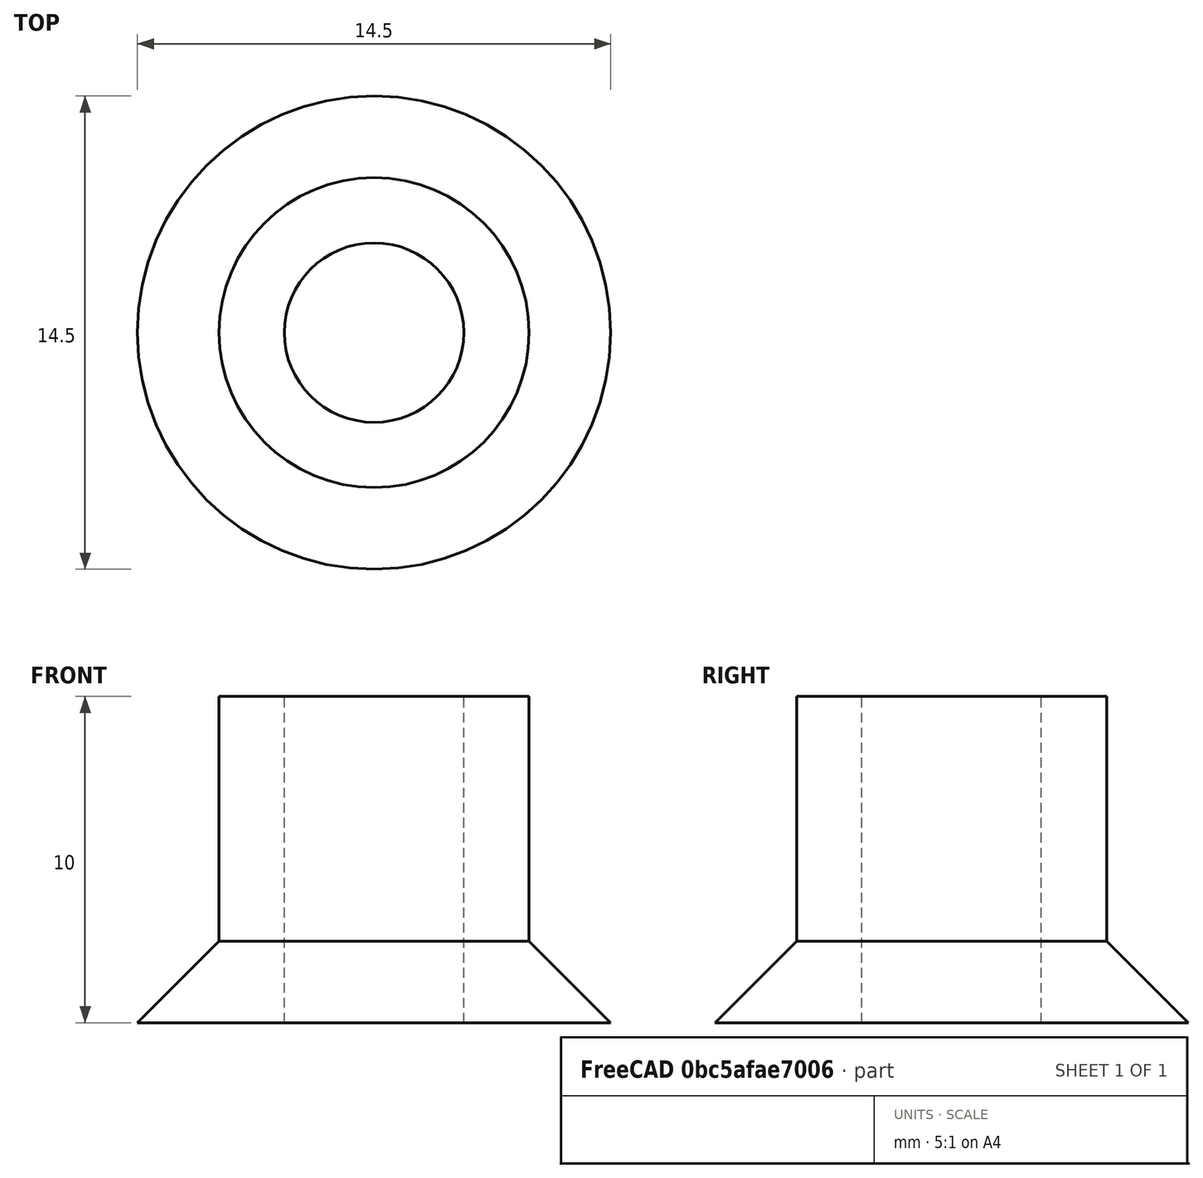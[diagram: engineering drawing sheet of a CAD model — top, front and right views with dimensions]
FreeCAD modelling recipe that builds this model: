
FCSTD DOCUMENT  (FreeCAD 0.19R24267 +148 (Git))
Label: Roller spacer long
License: All rights reserved
LicenseURL: http://en.wikipedia.org/wiki/All_rights_reserved
objects: Sketcher::SketchObject×1, PartDesign::Revolution×1, PartDesign::Body×1
note: 4 computed .brp shape members not serialized (recipe doc carries the construction recipe); baked Part::Feature solids carry a one-line shape summary decoded from their .brp

FEATURE [Sketcher::SketchObject] Sketch
  FullyConstrained = false
  MapMode = 5
  Placement = pos=(0,0,0) rot=(1,0,0;1.5708rad)
  Support = -> [XZ_Plane]
  sketch-geometry (7):
    g0: LineSegment StartX=2.75 StartY=0 StartZ=0 EndX=2.75 EndY=10 EndZ=0
    g1: LineSegment StartX=2.75 StartY=10 StartZ=0 EndX=4.75 EndY=10 EndZ=0
    g2: LineSegment StartX=4.75 StartY=10 StartZ=0 EndX=4.75 EndY=2.5 EndZ=0
    g3: LineSegment StartX=4.75 StartY=2.5 StartZ=0 EndX=7.25 EndY=0 EndZ=0
    g4: LineSegment StartX=2.75 StartY=0 StartZ=0 EndX=7.25 EndY=0 EndZ=0
    g5: LineSegment StartX=2.75 StartY=0 StartZ=0 EndX=0 EndY=0 EndZ=0
    g6: LineSegment StartX=0 StartY=0 StartZ=0 EndX=0 EndY=8.34893 EndZ=0
  constraints (19):
    c: PointOnObject(g0,g-1)
    c: Vertical(g0)
    c: Horizontal(g1)
    c: Coincident(g2,g1)
    c: Vertical(g2)
    c: Coincident(g3,g2)
    c: PointOnObject(g3,g-1)
    c: Coincident(g4,g0)
    c: Coincident(g4,g3)
    c: Coincident(g5,g0)
    c: Coincident(g5,g-1)
    c: DistanceX(g5,g5) = 2.75
    c: Coincident(g1,g0)
    c: DistanceX(g1,g1) = 2
    c: Angle(g3,g2) = 2.35619
    c: DistanceX(g2,g3) = 2.5
    c: DistanceY(g0,g0) = 10
    c: Coincident(g6,g-1)
    c: PointOnObject(g6,g-2)
FEATURE [PartDesign::Revolution] Revolution
  Angle = 360
  Axis = (0,-2e-16,1)
  Base = (0,0,0)
  Placement = pos=(0,0,0) rot=(1,0,0;1.5708rad)
  Profile = -> Sketch
  ReferenceAxis = -> Sketch [V_Axis]
  Reversed = true
FEATURE [PartDesign::Body] Body
  Group = -> [Sketch,Revolution]
  Origin = -> Origin
  Tip = -> Revolution
